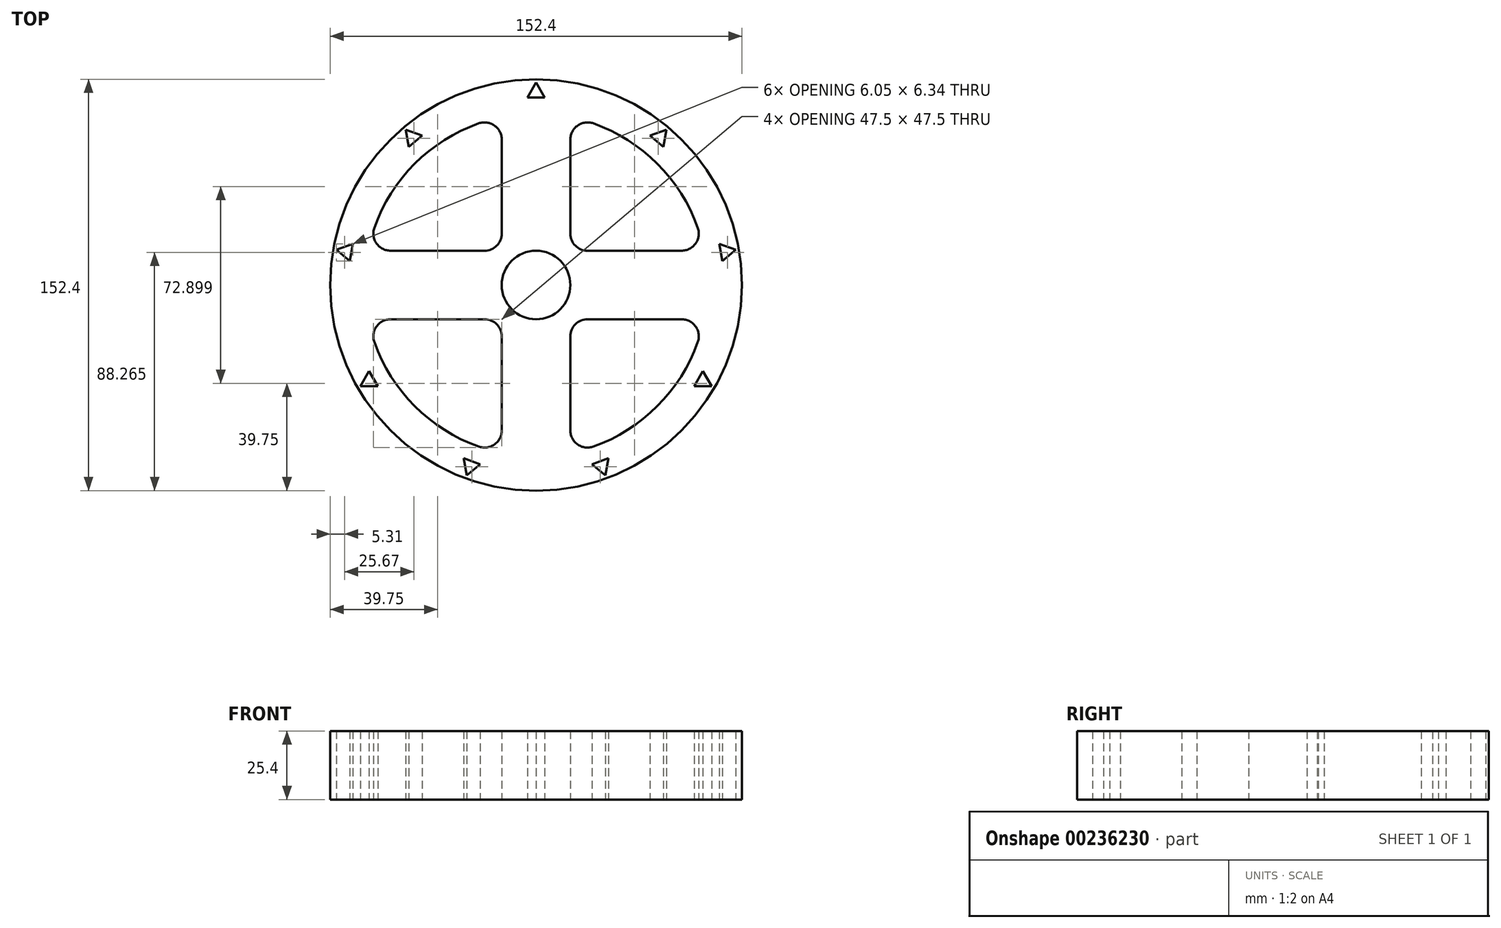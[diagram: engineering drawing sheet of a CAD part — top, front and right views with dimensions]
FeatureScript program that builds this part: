
annotation { "Feature Type Name" : "Feature", "Feature Type Description" : "" }
export const myFeature = defineFeature(function(context is Context, id is Id, definition is map)
    precondition{}
    {
        {
            var Q0;
            Q0=qCreatedBy(makeId("Top.planeOp"),FACE);
            var sketch = newSketch(context, id + "F0", { "sketchPlane" : qUnion([Q0])});
            skCircle(sketch, "E0", {"center": v(0, 0) * mm, "radius": 76.2 * mm});
            skArc(sketch, "E1", {"start": v(-21.17, 59.87) * mm, "mid": v(-44.9, 44.9) * mm, "end": v(-59.87, 21.17) * mm});
            skCircle(sketch, "E2", {"center": v(0, 0) * mm, "radius": 12.7 * mm});
            skLineSegment(sketch, "E3", {"start": v(0, 0) * mm, "end": v(0, 63.5) * mm});
            skLineSegment(sketch, "E4.0", {"start": v(-12.7, 19.05) * mm, "end": v(-12.7, 34.77) * mm});
            skLineSegment(sketch, "E5.0", {"start": v(12.7, 19.05) * mm, "end": v(12.7, 34.77) * mm});
            skLineSegment(sketch, "E6", {"start": v(0, 0) * mm, "end": v(37.02, 0) * mm});
            skLineSegment(sketch, "E7", {"start": v(0, 0) * mm, "end": v(0, -63.5) * mm});
            skLineSegment(sketch, "E8", {"start": v(0, 0) * mm, "end": v(-37.02, 0) * mm});
            skLineSegment(sketch, "E9.0", {"start": v(-19.05, 12.7) * mm, "end": v(-34.77, 12.7) * mm});
            skLineSegment(sketch, "E10.0", {"start": v(-19.05, -12.7) * mm, "end": v(-34.77, -12.7) * mm});
            skLineSegment(sketch, "E11.0", {"start": v(19.05, -12.7) * mm, "end": v(34.77, -12.7) * mm});
            skLineSegment(sketch, "E12.0", {"start": v(19.05, 12.7) * mm, "end": v(34.77, 12.7) * mm});
            skLineSegment(sketch, "E13.0", {"start": v(12.7, -19.05) * mm, "end": v(12.7, -34.77) * mm});
            skLineSegment(sketch, "E14.0", {"start": v(-12.7, -19.05) * mm, "end": v(-12.7, -34.77) * mm});
            skLineSegment(sketch, "E15.trimOffspring", {"start": v(-75.13, 12.7) * mm, "end": v(-76.2, 12.7) * mm});
            skLineSegment(sketch, "E16.trimOffspring", {"start": v(-75.13, -12.7) * mm, "end": v(-76.2, -12.7) * mm});
            skLineSegment(sketch, "E17.trimOffspring", {"start": v(-12.7, -75.13) * mm, "end": v(-12.7, -76.2) * mm});
            skLineSegment(sketch, "E18.trimOffspring", {"start": v(12.7, -75.13) * mm, "end": v(12.7, -76.2) * mm});
            skLineSegment(sketch, "E19.trimOffspring", {"start": v(75.13, -12.7) * mm, "end": v(76.2, -12.7) * mm});
            skLineSegment(sketch, "E20.trimOffspring", {"start": v(75.13, 12.7) * mm, "end": v(76.2, 12.7) * mm});
            skLineSegment(sketch, "E21.trimOffspring", {"start": v(12.7, 75.13) * mm, "end": v(12.7, 76.2) * mm});
            skLineSegment(sketch, "E22.trimOffspring", {"start": v(-12.7, 75.13) * mm, "end": v(-12.7, 76.2) * mm});
            skArc(sketch, "E23.trimOffspring", {"start": v(59.87, 21.17) * mm, "mid": v(44.9, 44.9) * mm, "end": v(21.17, 59.87) * mm});
            skArc(sketch, "E24.trimOffspring", {"start": v(21.17, -59.87) * mm, "mid": v(44.9, -44.9) * mm, "end": v(59.87, -21.17) * mm});
            skArc(sketch, "E25.trimOffspring", {"start": v(-59.87, -21.17) * mm, "mid": v(-44.9, -44.9) * mm, "end": v(-21.17, -59.87) * mm});
            skPoint(sketch, "E26.visualSharp", {"position": v(-12.7, 12.7) * mm});
            skArc(sketch, "E26.filletArc", {"start": v(-19.05, 12.7) * mm, "mid": v(-14.56, 14.56) * mm, "end": v(-12.7, 19.05) * mm});
            skPoint(sketch, "E27.visualSharp", {"position": v(12.7, 12.7) * mm});
            skArc(sketch, "E27.filletArc", {"start": v(12.7, 19.05) * mm, "mid": v(14.56, 14.56) * mm, "end": v(19.05, 12.7) * mm});
            skPoint(sketch, "E28.visualSharp", {"position": v(12.7, -12.7) * mm});
            skArc(sketch, "E28.filletArc", {"start": v(19.05, -12.7) * mm, "mid": v(14.56, -14.56) * mm, "end": v(12.7, -19.05) * mm});
            skPoint(sketch, "E29.visualSharp", {"position": v(-12.7, -12.7) * mm});
            skArc(sketch, "E29.filletArc", {"start": v(-12.7, -19.05) * mm, "mid": v(-14.56, -14.56) * mm, "end": v(-19.05, -12.7) * mm});
            skPoint(sketch, "E30.visualSharp", {"position": v(-62.22, 12.7) * mm});
            skArc(sketch, "E30.filletArc", {"start": v(-59.87, 21.17) * mm, "mid": v(-59.07, 15.38) * mm, "end": v(-53.88, 12.7) * mm});
            skPoint(sketch, "E31.visualSharp", {"position": v(-12.7, 62.22) * mm});
            skArc(sketch, "E31.filletArc", {"start": v(-12.7, 53.88) * mm, "mid": v(-15.38, 59.07) * mm, "end": v(-21.17, 59.87) * mm});
            skPoint(sketch, "E32.visualSharp", {"position": v(12.7, 62.22) * mm});
            skArc(sketch, "E32.filletArc", {"start": v(21.17, 59.87) * mm, "mid": v(15.38, 59.07) * mm, "end": v(12.7, 53.88) * mm});
            skPoint(sketch, "E33.visualSharp", {"position": v(62.22, 12.7) * mm});
            skArc(sketch, "E33.filletArc", {"start": v(53.88, 12.7) * mm, "mid": v(59.07, 15.38) * mm, "end": v(59.87, 21.17) * mm});
            skPoint(sketch, "E34.visualSharp", {"position": v(62.22, -12.7) * mm});
            skArc(sketch, "E34.filletArc", {"start": v(59.87, -21.17) * mm, "mid": v(59.07, -15.38) * mm, "end": v(53.88, -12.7) * mm});
            skPoint(sketch, "E35.visualSharp", {"position": v(12.7, -62.22) * mm});
            skArc(sketch, "E35.filletArc", {"start": v(12.7, -53.88) * mm, "mid": v(15.38, -59.07) * mm, "end": v(21.17, -59.87) * mm});
            skPoint(sketch, "E36.visualSharp", {"position": v(-12.7, -62.22) * mm});
            skArc(sketch, "E36.filletArc", {"start": v(-21.17, -59.87) * mm, "mid": v(-15.38, -59.07) * mm, "end": v(-12.7, -53.88) * mm});
            skPoint(sketch, "E37.visualSharp", {"position": v(-62.22, -12.7) * mm});
            skArc(sketch, "E37.filletArc", {"start": v(-53.88, -12.7) * mm, "mid": v(-59.07, -15.38) * mm, "end": v(-59.87, -21.17) * mm});
            skCircle(sketch, "E38.cCircle", {"center": v(0, 71.34) * mm, "radius": 1.86 * mm, "construction": true});
            skLineSegment(sketch, "E38.0", {"start": v(3.22, 69.48) * mm, "end": v(-3.22, 69.48) * mm});
            skLineSegment(sketch, "E38.1", {"start": v(-3.22, 69.48) * mm, "end": v(0, 75.05) * mm});
            skLineSegment(sketch, "E38.2", {"start": v(0, 75.05) * mm, "end": v(3.22, 69.48) * mm});
            skPoint(sketch, "E38.0.midPoint", {"position": v(0, 69.48) * mm});
            skLineSegment(sketch, "E39.1.0", {"start": v(47.13, 51.16) * mm, "end": v(42.2, 55.3) * mm});
            skLineSegment(sketch, "E39.1.1", {"start": v(48.24, 57.5) * mm, "end": v(47.13, 51.16) * mm});
            skLineSegment(sketch, "E39.1.2", {"start": v(42.2, 55.3) * mm, "end": v(48.24, 57.5) * mm});
            skLineSegment(sketch, "E39.2.0", {"start": v(68.98, 8.9) * mm, "end": v(67.87, 15.23) * mm});
            skLineSegment(sketch, "E39.2.1", {"start": v(73.91, 13.03) * mm, "end": v(68.98, 8.9) * mm});
            skLineSegment(sketch, "E39.2.2", {"start": v(67.87, 15.23) * mm, "end": v(73.91, 13.03) * mm});
            skLineSegment(sketch, "E39.3.0", {"start": v(58.56, -37.53) * mm, "end": v(61.78, -31.95) * mm});
            skLineSegment(sketch, "E39.3.1", {"start": v(65, -37.53) * mm, "end": v(58.56, -37.53) * mm});
            skLineSegment(sketch, "E39.3.2", {"start": v(61.78, -31.95) * mm, "end": v(65, -37.53) * mm});
            skLineSegment(sketch, "E39.4.0", {"start": v(20.74, -66.4) * mm, "end": v(26.79, -64.19) * mm});
            skLineSegment(sketch, "E39.4.1", {"start": v(25.67, -70.53) * mm, "end": v(20.74, -66.4) * mm});
            skLineSegment(sketch, "E39.4.2", {"start": v(26.79, -64.19) * mm, "end": v(25.67, -70.53) * mm});
            skLineSegment(sketch, "E39.5.0", {"start": v(-26.79, -64.19) * mm, "end": v(-20.74, -66.4) * mm});
            skLineSegment(sketch, "E39.5.1", {"start": v(-25.67, -70.53) * mm, "end": v(-26.79, -64.19) * mm});
            skLineSegment(sketch, "E39.5.2", {"start": v(-20.74, -66.4) * mm, "end": v(-25.67, -70.53) * mm});
            skLineSegment(sketch, "E39.6.0", {"start": v(-61.78, -31.95) * mm, "end": v(-58.56, -37.53) * mm});
            skLineSegment(sketch, "E39.6.1", {"start": v(-65, -37.53) * mm, "end": v(-61.78, -31.95) * mm});
            skLineSegment(sketch, "E39.6.2", {"start": v(-58.56, -37.53) * mm, "end": v(-65, -37.53) * mm});
            skLineSegment(sketch, "E39.7.0", {"start": v(-67.87, 15.23) * mm, "end": v(-68.98, 8.9) * mm});
            skLineSegment(sketch, "E39.7.1", {"start": v(-73.91, 13.03) * mm, "end": v(-67.87, 15.23) * mm});
            skLineSegment(sketch, "E39.7.2", {"start": v(-68.98, 8.9) * mm, "end": v(-73.91, 13.03) * mm});
            skLineSegment(sketch, "E39.8.0", {"start": v(-42.2, 55.3) * mm, "end": v(-47.13, 51.16) * mm});
            skLineSegment(sketch, "E39.8.1", {"start": v(-48.24, 57.5) * mm, "end": v(-42.2, 55.3) * mm});
            skLineSegment(sketch, "E39.8.2", {"start": v(-47.13, 51.16) * mm, "end": v(-48.24, 57.5) * mm});
            skLineSegment(sketch, "E39.anchor1", {"start": v(0, 0) * mm, "end": v(-0.59, 12.69) * mm, "construction": true});
            skLineSegment(sketch, "E39.anchor2", {"start": v(0, 0) * mm, "end": v(-47.13, 51.16) * mm, "construction": true});
            skArc(sketch, "E40", {"start": v(-12.7, 45.84) * mm, "mid": v(-33.63, 33.63) * mm, "end": v(-45.84, 12.7) * mm});
            skArc(sketch, "E41", {"start": v(-12.7, 34.77) * mm, "mid": v(-26.18, 26.18) * mm, "end": v(-34.77, 12.7) * mm});
            skLineSegment(sketch, "E42.trimOffspring", {"start": v(-12.7, 45.84) * mm, "end": v(-12.7, 53.88) * mm});
            skLineSegment(sketch, "E43.trimOffspring", {"start": v(12.7, 45.84) * mm, "end": v(12.7, 53.88) * mm});
            skLineSegment(sketch, "E44.trimOffspring", {"start": v(45.84, 12.7) * mm, "end": v(53.88, 12.7) * mm});
            skLineSegment(sketch, "E45.trimOffspring", {"start": v(45.84, -12.7) * mm, "end": v(53.88, -12.7) * mm});
            skLineSegment(sketch, "E46.trimOffspring", {"start": v(12.7, -45.84) * mm, "end": v(12.7, -53.88) * mm});
            skLineSegment(sketch, "E47.trimOffspring", {"start": v(-12.7, -45.84) * mm, "end": v(-12.7, -53.88) * mm});
            skLineSegment(sketch, "E48.trimOffspring", {"start": v(-45.84, -12.7) * mm, "end": v(-53.88, -12.7) * mm});
            skLineSegment(sketch, "E49.trimOffspring", {"start": v(-45.84, 12.7) * mm, "end": v(-53.88, 12.7) * mm});
            skLineSegment(sketch, "E50.trimOffspring", {"start": v(-47.57, 0) * mm, "end": v(-63.5, 0) * mm});
            skLineSegment(sketch, "E51.trimOffspring", {"start": v(47.57, 0) * mm, "end": v(63.5, 0) * mm});
            skLineSegment(sketch, "E52", {"start": v(-12.7, 45.84) * mm, "end": v(-12.7, 34.77) * mm});
            skLineSegment(sketch, "E53", {"start": v(12.7, 45.84) * mm, "end": v(12.7, 34.77) * mm});
            skLineSegment(sketch, "E54", {"start": v(34.77, 12.7) * mm, "end": v(45.84, 12.7) * mm});
            skLineSegment(sketch, "E55", {"start": v(45.84, -12.7) * mm, "end": v(34.77, -12.7) * mm});
            skLineSegment(sketch, "E56", {"start": v(12.7, -34.77) * mm, "end": v(12.7, -45.84) * mm});
            skLineSegment(sketch, "E57", {"start": v(-12.7, -45.84) * mm, "end": v(-12.7, -34.77) * mm});
            skLineSegment(sketch, "E58", {"start": v(-34.77, -12.7) * mm, "end": v(-45.84, -12.7) * mm});
            skLineSegment(sketch, "E59", {"start": v(-45.84, 12.7) * mm, "end": v(-34.77, 12.7) * mm});
            skArc(sketch, "E60.trimOffspring", {"start": v(34.77, 12.7) * mm, "mid": v(26.18, 26.18) * mm, "end": v(12.7, 34.77) * mm});
            skArc(sketch, "E61.trimOffspring", {"start": v(45.84, 12.7) * mm, "mid": v(33.63, 33.63) * mm, "end": v(12.7, 45.84) * mm});
            skArc(sketch, "E62.trimOffspring", {"start": v(12.7, -34.77) * mm, "mid": v(26.18, -26.18) * mm, "end": v(34.77, -12.7) * mm});
            skArc(sketch, "E63.trimOffspring", {"start": v(12.7, -45.84) * mm, "mid": v(33.63, -33.63) * mm, "end": v(45.84, -12.7) * mm});
            skArc(sketch, "E64.trimOffspring", {"start": v(-45.84, -12.7) * mm, "mid": v(-33.63, -33.63) * mm, "end": v(-12.7, -45.84) * mm});
            skArc(sketch, "E65.trimOffspring", {"start": v(-34.77, -12.7) * mm, "mid": v(-26.18, -26.18) * mm, "end": v(-12.7, -34.77) * mm});
            skSolve(sketch);
        }
        {
            var Q0;
            Q0 = qSketchRegion(id + "F0", true);
            extrude(context, id + "F1", {"entities" : qUnion([Q0]), "endBound" : BoundingType.SYMMETRIC, "depth" : 25.4 * mm});
        }
    });
